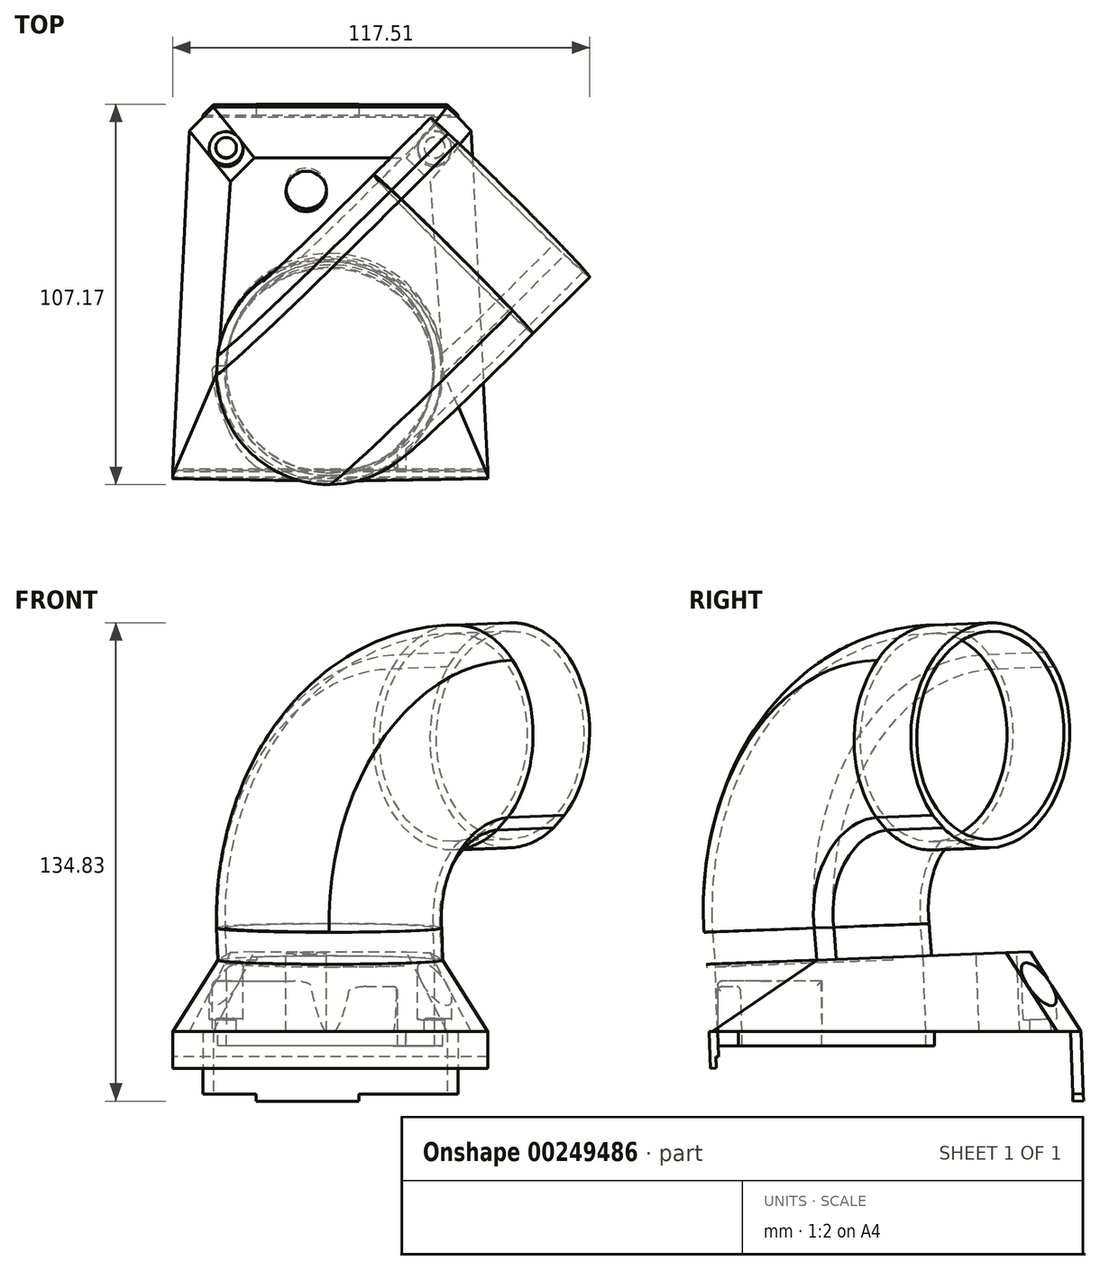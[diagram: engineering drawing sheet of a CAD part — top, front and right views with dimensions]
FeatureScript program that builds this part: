
annotation { "Feature Type Name" : "Feature", "Feature Type Description" : "" }
export const myFeature = defineFeature(function(context is Context, id is Id, definition is map)
    precondition{}
    {
        {
            var Q0;
            Q0=qCreatedBy(makeId("Top.planeOp"),FACE);
            var sketch = newSketch(context, id + "F0", { "sketchPlane" : qUnion([Q0])});
            skLineSegment(sketch, "E0", {"start": v(-32.94, 52.39) * mm, "end": v(32.94, 52.39) * mm});
            skLineSegment(sketch, "E1", {"start": v(32.94, 52.39) * mm, "end": v(39.68, 45.65) * mm});
            skLineSegment(sketch, "E2", {"start": v(39.68, 45.65) * mm, "end": v(44.4, -51.56) * mm});
            skLineSegment(sketch, "E3", {"start": v(43.62, -52.39) * mm, "end": v(-43.62, -52.39) * mm});
            skLineSegment(sketch, "E4", {"start": v(-44.4, -51.56) * mm, "end": v(-39.68, 45.65) * mm});
            skLineSegment(sketch, "E5", {"start": v(-39.68, 45.65) * mm, "end": v(-32.94, 52.39) * mm});
            skLineSegment(sketch, "E6", {"start": v(0, 0) * mm, "end": v(-41.9, 0) * mm, "construction": true});
            skLineSegment(sketch, "E7", {"start": v(0, 0) * mm, "end": v(41.9, 0) * mm, "construction": true});
            skLineSegment(sketch, "E8", {"start": v(0, 0) * mm, "end": v(0, -52.39) * mm, "construction": true});
            skLineSegment(sketch, "E9", {"start": v(0, 0) * mm, "end": v(0, 52.39) * mm, "construction": true});
            skPoint(sketch, "E10", {"position": v(0, -20.66) * mm});
            skPoint(sketch, "E11.visualSharp", {"position": v(-44.45, -52.39) * mm});
            skArc(sketch, "E11.filletArc", {"start": v(-44.4, -51.56) * mm, "mid": v(-44.2, -52.14) * mm, "end": v(-43.62, -52.39) * mm});
            skPoint(sketch, "E12.visualSharp", {"position": v(44.45, -52.39) * mm});
            skArc(sketch, "E12.filletArc", {"start": v(43.62, -52.39) * mm, "mid": v(44.2, -52.14) * mm, "end": v(44.4, -51.56) * mm});
            skSolve(sketch);
        }
        {
            var Q0;
            Q0=qCreatedBy(makeId("Right.planeOp"),FACE);
            var sketch = newSketch(context, id + "F1", { "sketchPlane" : qUnion([Q0])});
            skPoint(sketch, "E13.0", {"position": v(52.39, 0) * mm});
            skPoint(sketch, "E14.0", {"position": v(-51.56, 0) * mm});
            skLineSegment(sketch, "E15", {"start": v(52.39, 0) * mm, "end": v(52.39, 23.02) * mm, "construction": true});
            skLineSegment(sketch, "E16", {"start": v(-51.56, 0) * mm, "end": v(-51.56, 19.05) * mm, "construction": true});
            skSolve(sketch);
        }
        {
            var Q0;
            Q0=qCreatedBy(makeId("Top.planeOp"),FACE);
            cPlane(context, id + "F2", {"entities" : qUnion([Q0]), "cplaneType" : CPlaneType.OFFSET, "offset" : 23.02 * mm, "width" : 152.4 * mm, "height" : 152.4 * mm});
        }
        {
            var Q0;
            Q0=qCreatedBy(id+"F2.planeOp",FACE);
            var sketch = newSketch(context, id + "F3", { "sketchPlane" : qUnion([Q0])});
            skPoint(sketch, "E17.0", {"position": v(0, 52.39) * mm});
            skLineSegment(sketch, "E18", {"start": v(0, 52.39) * mm, "end": v(20.13, 52.39) * mm, "construction": true});
            skSolve(sketch);
        }
        {
            var Q0;
            Q0=sQuery(id+"F3.wireOp",EDGE,"E18");
            var Q1;
            Q1=sQuery(id+"F1.wireOp",VERTEX,"E16.end");
            cPlane(context, id + "F4", {"entities" : qUnion([Q0, Q1]), "cplaneType" : CPlaneType.LINE_ANGLE, "offset" : 25.4 * mm, "angle" : 0 * degree, "width" : 152.4 * mm, "height" : 152.4 * mm});
        }
        {
            var Q0;
            Q0=qCreatedBy(id+"F4.planeOp",FACE);
            var sketch = newSketch(context, id + "F5", { "sketchPlane" : qUnion([Q0])});
            skCircle(sketch, "E19", {"center": v(0, 20.65) * mm, "radius": 29.34 * mm, "construction": true});
            skArc(sketch, "E20", {"start": v(-31.72, 21.31) * mm, "mid": v(0, -11.08) * mm, "end": v(31.72, 21.32) * mm, "construction": true});
            skArc(sketch, "E21", {"start": v(31.72, 21.32) * mm, "mid": v(22.21, 43.3) * mm, "end": v(0.05, 52.37) * mm});
            skLineSegment(sketch, "E22", {"start": v(0, -11.08) * mm, "end": v(0, 49.98) * mm, "construction": true});
            skLineSegment(sketch, "E23", {"start": v(-21.43, -38.9) * mm, "end": v(21.43, -38.9) * mm});
            skLineSegment(sketch, "E24", {"start": v(21.43, -38.9) * mm, "end": v(28.17, -32.17) * mm});
            skLineSegment(sketch, "E25", {"start": v(28.17, -32.17) * mm, "end": v(31.72, 21.32) * mm});
            skLineSegment(sketch, "E26", {"start": v(-21.43, -38.9) * mm, "end": v(-28.16, -32.17) * mm});
            skLineSegment(sketch, "E27", {"start": v(-28.16, -32.17) * mm, "end": v(-31.72, 21.31) * mm});
            skArc(sketch, "E28", {"start": v(-0.04, 52.37) * mm, "mid": v(-22.2, 43.3) * mm, "end": v(-31.72, 21.31) * mm});
            skArc(sketch, "E29", {"start": v(0.05, 52.37) * mm, "mid": v(0, 52.37) * mm, "end": v(-0.04, 52.37) * mm});
            skSolve(sketch);
        }
        {
            var Q0;
            Q0=makeQuery(id+"F0.imprint","IMPRINT",FACE,{"disambiguationData":[TD([[makeQuery(id+"F0.imprint","IMPRINT",EDGE,{"derivedFrom":sQuery(id+"F0.wireOp",EDGE,"E0")}),-1.0]])]});
            var Q1;
            Q1=makeQuery(id+"F5.imprint","IMPRINT",FACE,{"disambiguationData":[TD([[makeQuery(id+"F5.imprint","IMPRINT",EDGE,{"derivedFrom":sQuery(id+"F5.wireOp",EDGE,"E21")}),1.0]])]});
            loft(context, id + "F6", {"sheetProfilesArray" : [{ "sheetProfileEntities" : qUnion([Q0]) }, { "sheetProfileEntities" : qUnion([Q1]) }]});
        }
        {
            var Q0;
            Q0=makeQuery(id+"F6.opLoft","CAP_FACE",FACE,{"disambiguationData":[OSD([makeQuery(id+"F5.imprint","IMPRINT",FACE,{"disambiguationData":[TD([[makeQuery(id+"F5.imprint","IMPRINT",EDGE,{"derivedFrom":sQuery(id+"F5.wireOp",EDGE,"E21")}),1.0]])]})])],"isStart":true});
            var sketch = newSketch(context, id + "F7", { "sketchPlane" : qUnion([Q0])});
            skCircle(sketch, "E30", {"center": v(0, -20.65) * mm, "radius": 29.34 * mm});
            skSolve(sketch);
        }
        {
            var Q0;
            Q0 = qSketchRegion(id + "F7", true);
            extrude(context, id + "F8", {"entities" : qUnion([Q0]), "operationType" : NewBodyOperationType.REMOVE, "endBound" : BoundingType.UP_TO_NEXT, "oppositeDirection" : true, "depth" : 25.4 * mm});
        }
        {
            var Q0;
            Q0=sQuery(id+"F0.wireOp",EDGE,"E3");
            var Q1;
            Q1=makeQuery(id+"F6.opLoft","CAP_FACE",FACE,{"disambiguationData":[OSD([makeQuery(id+"F5.imprint","IMPRINT",FACE,{"disambiguationData":[TD([[makeQuery(id+"F5.imprint","IMPRINT",EDGE,{"derivedFrom":sQuery(id+"F5.wireOp",EDGE,"E21")}),1.0]])]})])],"isStart":true});
            cPlane(context, id + "F9", {"entities" : qUnion([Q0, Q1]), "cplaneType" : CPlaneType.LINE_ANGLE, "offset" : 25.4 * mm, "angle" : 90 * degree, "width" : 152.4 * mm, "height" : 152.4 * mm});
        }
        {
            var Q0;
            Q0=qCreatedBy(id+"F9.planeOp",FACE);
            var sketch = newSketch(context, id + "F10", { "sketchPlane" : qUnion([Q0])});
            skLineSegment(sketch, "E31.0", {"start": v(43.62, 2) * mm, "end": v(-43.62, 2) * mm});
            skEllipticalArc(sketch, "E32.0", {});
            skEllipticalArc(sketch, "E33.0", {});
            skLineSegment(sketch, "E34.bottom", {"start": v(44.4, 1.97) * mm, "end": v(-44.4, 1.97) * mm});
            skLineSegment(sketch, "E34.top", {"start": v(44.4, -8.35) * mm, "end": v(-44.4, -8.35) * mm});
            skLineSegment(sketch, "E34.left", {"start": v(44.4, 1.97) * mm, "end": v(44.4, -8.35) * mm});
            skLineSegment(sketch, "E34.right", {"start": v(-44.4, 1.97) * mm, "end": v(-44.4, -8.35) * mm});
            const initialGuessF10  = {"E32.0": [-0.04361665668816759, 0.001968524113919549, 1, 0, 0.0007937500000000046, 3.0284986367993234e-05, 1.5707963267948966, 3.1902505879491185], "E33.0": [0.04361665668816731, 0.0019685241139195475, 1, 0, 0.0007937500000000028, 3.0284986367993163e-05, 6.234527372820301, 1.5707963267948966]};
            skSetInitialGuess(sketch, initialGuessF10);
            skSolve(sketch);
        }
        {
            var Q0;
            Q0 = qSketchRegion(id + "F10", true);
            extrude(context, id + "F11", {"entities" : qUnion([Q0]), "operationType" : NewBodyOperationType.ADD, "oppositeDirection" : true, "depth" : 2.4 * mm});
        }
        {
            var Q0;
            Q0=makeQuery(id+"F11.opExtrude","CAP_FACE",FACE,{"disambiguationData":[OSD([sQuery(id+"F10.wireOp",EDGE,"E31.0"),sQuery(id+"F10.wireOp",EDGE,"E32.0"),sQuery(id+"F10.wireOp",EDGE,"E33.0"),sQuery(id+"F10.wireOp",EDGE,"E34.top"),sQuery(id+"F10.wireOp",EDGE,"E34.left"),sQuery(id+"F10.wireOp",EDGE,"E34.right")])],"isStart":false});
            cPlane(context, id + "F12", {"entities" : qUnion([Q0]), "cplaneType" : CPlaneType.OFFSET, "offset" : 99.31 * mm, "width" : 152.4 * mm, "height" : 152.4 * mm});
        }
        {
            var Q0;
            Q0=qCreatedBy(id+"F12.planeOp",FACE);
            var sketch = newSketch(context, id + "F13", { "sketchPlane" : qUnion([Q0])});
            skLineSegment(sketch, "E35.0.6", {"start": v(-32.94, -2) * mm, "end": v(32.94, -2) * mm});
            skLineSegment(sketch, "E36.bottom", {"start": v(36.9, -2) * mm, "end": v(-36.9, -2) * mm});
            skLineSegment(sketch, "E36.top", {"start": v(36.9, -19.46) * mm, "end": v(-36.9, -19.46) * mm});
            skLineSegment(sketch, "E36.left", {"start": v(36.9, -2) * mm, "end": v(36.9, -19.46) * mm});
            skLineSegment(sketch, "E36.right", {"start": v(-36.9, -2) * mm, "end": v(-36.9, -19.46) * mm});
            skLineSegment(sketch, "E37", {"start": v(0, -19.46) * mm, "end": v(0, -2) * mm, "construction": true});
            skSolve(sketch);
        }
        {
            var Q0;
            Q0 = qSketchRegion(id + "F13", true);
            var Q1;
            Q1=sQuery(id+"F0.wireOp",VERTEX,"E0.start");
            extrude(context, id + "F14", {"entities" : qUnion([Q0]), "operationType" : NewBodyOperationType.ADD, "endBound" : BoundingType.UP_TO_VERTEX, "endBoundEntityVertex" : qUnion([Q1]), "depth" : 25.4 * mm});
        }
        {
            var Q0;
            Q0=makeQuery(id+"F14.opExtrude","SWEPT_FACE",FACE,{"disambiguationData":[OSD([sQuery(id+"F13.wireOp",EDGE,"E36.left")])]});
            var sketch = newSketch(context, id + "F15", { "sketchPlane" : qUnion([Q0])});
            skLineSegment(sketch, "E38.0", {"start": v(-45.65, 0) * mm, "end": v(-52.39, 0) * mm});
            skLineSegment(sketch, "E39.0.0", {"start": v(-49.4, -0.11) * mm, "end": v(-52.39, 0) * mm});
            skLineSegment(sketch, "E40", {"start": v(-49.4, -0.11) * mm, "end": v(-49.39, 0) * mm});
            skSolve(sketch);
        }
        {
            var Q0;
            Q0 = qSketchRegion(id + "F15", true);
            extrude(context, id + "F16", {"entities" : qUnion([Q0]), "operationType" : NewBodyOperationType.ADD, "oppositeDirection" : true, "depth" : 73.63 * mm});
        }
        {
            var Q0;
            Q0=makeQuery(id+"F14.opExtrude","SWEPT_FACE",FACE,{"disambiguationData":[OSD([sQuery(id+"F13.wireOp",EDGE,"E36.top")])]});
            var sketch = newSketch(context, id + "F17", { "sketchPlane" : qUnion([Q0])});
            skLineSegment(sketch, "E41.0", {"start": v(-35.94, -49.35) * mm, "end": v(-32.94, -52.35) * mm});
            skLineSegment(sketch, "E42", {"start": v(-32.94, -52.35) * mm, "end": v(-36.9, -52.35) * mm});
            skLineSegment(sketch, "E43", {"start": v(-36.9, -52.35) * mm, "end": v(-36.9, -49.35) * mm});
            skLineSegment(sketch, "E44", {"start": v(-36.9, -49.35) * mm, "end": v(-35.94, -49.35) * mm});
            skLineSegment(sketch, "E45.0", {"start": v(32.94, -52.35) * mm, "end": v(35.94, -49.35) * mm});
            skLineSegment(sketch, "E46", {"start": v(32.94, -52.35) * mm, "end": v(36.9, -52.35) * mm});
            skLineSegment(sketch, "E47", {"start": v(36.9, -52.35) * mm, "end": v(36.9, -49.35) * mm});
            skLineSegment(sketch, "E48", {"start": v(36.9, -49.35) * mm, "end": v(35.94, -49.35) * mm});
            skSolve(sketch);
        }
        {
            var Q0;
            Q0 = qSketchRegion(id + "F17", true);
            extrude(context, id + "F18", {"entities" : qUnion([Q0]), "operationType" : NewBodyOperationType.REMOVE, "endBound" : BoundingType.UP_TO_NEXT, "oppositeDirection" : true, "depth" : 25.4 * mm});
        }
        {
            var Q0;
            Q0=makeQuery(id+"F11.opExtrude","SWEPT_FACE",FACE,{"disambiguationData":[OSD([sQuery(id+"F10.wireOp",EDGE,"E34.top")])]});
            var sketch = newSketch(context, id + "F19", { "sketchPlane" : qUnion([Q0])});
            skEllipticalArc(sketch, "E49.0", {});
            skLineSegment(sketch, "E50.0", {"start": v(-44.4, 51.52) * mm, "end": v(-39.68, -45.62) * mm});
            skLineSegment(sketch, "E51", {"start": v(-44.4, 49.96) * mm, "end": v(-44.33, 49.96) * mm});
            skLineSegment(sketch, "E52", {"start": v(-44.4, 49.96) * mm, "end": v(-44.4, 51.52) * mm});
            skLineSegment(sketch, "E53", {"start": v(-44.4, 51.52) * mm, "end": v(-44.4, 52.35) * mm});
            skLineSegment(sketch, "E54", {"start": v(-44.4, 52.35) * mm, "end": v(-43.62, 52.35) * mm});
            const initialGuessF19  = {"E49.0": [-0.04361665668816758, 0.051556182479654336, -1, 0, 0.0007937500000000046, 0.000793172038148533, 4.712388980384686, 0.04865793435924814]};
            skSetInitialGuess(sketch, initialGuessF19);
            skSolve(sketch);
        }
        {
            var Q0;
            Q0=sQuery(id+"F0.wireOp",VERTEX,"E10");
            var Q1;
            Q1=qCreatedBy(id+"F9.planeOp",FACE);
            cPlane(context, id + "F20", {"entities" : qUnion([Q0, Q1]), "cplaneType" : CPlaneType.PLANE_POINT, "offset" : 25.4 * mm, "width" : 152.4 * mm, "height" : 152.4 * mm});
        }
        {
            var Q0;
            Q0=qCreatedBy(id+"F20.planeOp",FACE);
            var Q1;
            Q1=qCreatedBy(makeId("Right.planeOp"),FACE);
            cPlane(context, id + "F21", {"entities" : qUnion([Q0, Q1]), "cplaneType" : CPlaneType.MID_PLANE, "offset" : 25.4 * mm, "flipAlignment" : true, "width" : 152.4 * mm, "height" : 152.4 * mm});
        }
        {
            var Q0;
            Q0=qCreatedBy(id+"F21.planeOp",FACE);
            var sketch = newSketch(context, id + "F22", { "sketchPlane" : qUnion([Q0])});
            skLineSegment(sketch, "E55.0", {"start": v(-45, 18.6) * mm, "end": v(13.58, 21.77) * mm, "construction": true});
            skLineSegment(sketch, "E56", {"start": v(-15.71, 20.19) * mm, "end": v(-16.24, 30.05) * mm});
            skLineSegment(sketch, "E57", {"start": v(34.48, 83.6) * mm, "end": v(57.06, 83.6) * mm});
            skPoint(sketch, "E58.visualSharp", {"position": v(-19.14, 83.6) * mm});
            skArc(sketch, "E58.filletArc", {"start": v(34.48, 83.6) * mm, "mid": v(-2.4, 67.73) * mm, "end": v(-16.24, 30.05) * mm});
            skSolve(sketch);
        }
        {
            var Q0;
            Q0=makeQuery(id+"F6.opLoft","CAP_FACE",FACE,{"disambiguationData":[OSD([makeQuery(id+"F5.imprint","IMPRINT",FACE,{"disambiguationData":[TD([[makeQuery(id+"F5.imprint","IMPRINT",EDGE,{"derivedFrom":sQuery(id+"F5.wireOp",EDGE,"E21")}),1.0]])]})])],"isStart":true});
            var sketch = newSketch(context, id + "F23", { "sketchPlane" : qUnion([Q0])});
            skCircle(sketch, "E59.0", {"center": v(0, -20.65) * mm, "radius": 29.34 * mm});
            skFitSpline(sketch, "E60.0", {"points": [v(-31.72, -21.31) * mm, v(-31.67, -23.37) * mm, v(-31.43, -25.4) * mm, v(-31, -27.4) * mm, v(-30.56, -29.4) * mm, v(-29.93, -31.36) * mm, v(-29.12, -33.24) * mm, v(-28.3, -35.12) * mm, v(-27.31, -36.91) * mm, v(-26.15, -38.6) * mm, v(-25, -40.3) * mm, v(-23.68, -41.86) * mm, v(-22.2, -43.3) * mm, v(-20.74, -44.74) * mm, v(-19.15, -46.02) * mm, v(-17.44, -47.15) * mm, v(-15.72, -48.28) * mm, v(-13.91, -49.23) * mm, v(-12.01, -50.01) * mm, v(-10.11, -50.79) * mm, v(-8.16, -51.38) * mm, v(-6.14, -51.77) * mm, v(-4.13, -52.17) * mm, v(-2.1, -52.37) * mm, v(-0.04, -52.37) * mm]});
            skCircle(sketch, "E61", {"center": v(0, -20.65) * mm, "radius": 31.72 * mm});
            skSolve(sketch);
        }
        {
            var Q0;
            Q0=makeQuery(id+"F23.imprint","IMPRINT",FACE,{"disambiguationData":[TD([[makeQuery(id+"F23.imprint","IMPRINT",EDGE,{"derivedFrom":sQuery(id+"F23.wireOp",EDGE,"E59.0")}),-1.0]])]});
            var Q1;
            Q1=sQuery(id+"F22.wireOp",EDGE,"E56");
            var Q2;
            Q2=sQuery(id+"F22.wireOp",EDGE,"E58.filletArc");
            var Q3;
            Q3=sQuery(id+"F22.wireOp",EDGE,"E57");
            sweep(context, id + "F24", {"operationType" : NewBodyOperationType.ADD, "profiles" : qUnion([Q0]), "path" : qUnion([Q1, Q2, Q3])});
        }
        {
            var Q0;
            {var subQ1=sQuery(id+"F5.wireOp",EDGE,"E24");var subQ2=sQuery(id+"F5.wireOp",EDGE,"E23");var subQ5=sQuery(id+"F5.wireOp",EDGE,"E26");Q0=makeQuery(id+"F23.imprint","IMPRINT",FACE,{"disambiguationData":[TD([[makeQuery(id+"F23.imprint","IMPRINT",EDGE,{"derivedFrom":makeQuery(id+"F6.opLoft","MID_CAP_EDGE",EDGE,{"disambiguationData":[OSD([subQ2,subQ1,subQ5])],"capPos":1.0})}),1.0]])]});}
            var sketch = newSketch(context, id + "F25", { "sketchPlane" : qUnion([Q0])});
            skLineSegment(sketch, "E62.0", {"start": v(-44.4, -51.52) * mm, "end": v(-39.68, 45.62) * mm, "construction": true});
            skLineSegment(sketch, "E63.0", {"start": v(39.68, 45.62) * mm, "end": v(44.4, -51.52) * mm, "construction": true});
            skLineSegment(sketch, "E64.0", {"start": v(35.94, 49.35) * mm, "end": v(-35.94, 49.35) * mm, "construction": true});
            skLineSegment(sketch, "E65", {"start": v(-39.9, 40.97) * mm, "end": v(39.9, 40.97) * mm, "construction": true});
            skCircle(sketch, "E66", {"center": v(-29.36, 40.97) * mm, "radius": 2.92 * mm});
            skCircle(sketch, "E67", {"center": v(29.39, 40.97) * mm, "radius": 2.92 * mm});
            skSolve(sketch);
        }
        {
            var Q0;
            Q0 = qSketchRegion(id + "F25", true);
            var Q1;
            Q1=makeQuery(id+"F6.opLoft","CAP_FACE",FACE,{"disambiguationData":[OSD([makeQuery(id+"F0.imprint","IMPRINT",FACE,{"disambiguationData":[TD([[makeQuery(id+"F0.imprint","IMPRINT",EDGE,{"derivedFrom":sQuery(id+"F0.wireOp",EDGE,"E0")}),-1.0]])]})])],"isStart":true});
            extrude(context, id + "F26", {"entities" : qUnion([Q0]), "operationType" : NewBodyOperationType.REMOVE, "endBound" : BoundingType.UP_TO_SURFACE, "oppositeDirection" : true, "endBoundEntityFace" : qUnion([Q1]), "depth" : 25.4 * mm});
        }
        {
            var Q0;
            {var subQ1=sQuery(id+"F5.wireOp",EDGE,"E24");var subQ2=sQuery(id+"F5.wireOp",EDGE,"E23");var subQ5=sQuery(id+"F5.wireOp",EDGE,"E26");Q0=makeQuery(id+"F23.imprint","IMPRINT",FACE,{"disambiguationData":[TD([[makeQuery(id+"F23.imprint","IMPRINT",EDGE,{"derivedFrom":makeQuery(id+"F6.opLoft","MID_CAP_EDGE",EDGE,{"disambiguationData":[OSD([subQ2,subQ1,subQ5])],"capPos":1.0})}),1.0]])]});}
            var sketch = newSketch(context, id + "F27", { "sketchPlane" : qUnion([Q0])});
            skCircle(sketch, "E68.0", {"center": v(-29.36, 40.97) * mm, "radius": 2.92 * mm});
            skCircle(sketch, "E69.0", {"center": v(29.39, 40.97) * mm, "radius": 2.92 * mm});
            skCircle(sketch, "E70", {"center": v(-29.36, 40.97) * mm, "radius": 4.76 * mm});
            skCircle(sketch, "E71", {"center": v(29.39, 40.97) * mm, "radius": 4.76 * mm});
            skSolve(sketch);
        }
        {
            var Q0;
            Q0 = qSketchRegion(id + "F27", true);
            extrude(context, id + "F28", {"entities" : qUnion([Q0]), "operationType" : NewBodyOperationType.REMOVE, "oppositeDirection" : true, "depth" : 19.05 * mm});
        }
        {
            var Q0;
            Q0=makeQuery(id+"F6.opLoft","CAP_FACE",FACE,{"disambiguationData":[OSD([makeQuery(id+"F5.imprint","IMPRINT",FACE,{"disambiguationData":[TD([[makeQuery(id+"F5.imprint","IMPRINT",EDGE,{"derivedFrom":sQuery(id+"F5.wireOp",EDGE,"E21")}),1.0]])]})])],"isStart":true});
            var sketch = newSketch(context, id + "F29", { "sketchPlane" : qUnion([Q0])});
            skLineSegment(sketch, "E72.0", {"start": v(-28.16, 32.17) * mm, "end": v(-31.35, -15.8) * mm});
            skLineSegment(sketch, "E73.0", {"start": v(31.35, -15.8) * mm, "end": v(28.17, 32.17) * mm});
            skLineSegment(sketch, "E74.0", {"start": v(21.43, 38.9) * mm, "end": v(-21.43, 38.9) * mm});
            skLineSegment(sketch, "E75", {"start": v(-28.35, 29.38) * mm, "end": v(28.35, 29.38) * mm, "construction": true});
            skCircle(sketch, "E76", {"center": v(-6.76, 29.38) * mm, "radius": 5.72 * mm});
            skSolve(sketch);
        }
        {
            var Q0;
            Q0=makeQuery(id+"F29.imprint","IMPRINT",FACE,{"disambiguationData":[TD([[makeQuery(id+"F29.imprint","IMPRINT",EDGE,{"derivedFrom":sQuery(id+"F29.wireOp",EDGE,"E76")}),1.0]])]});
            var Q1;
            Q1 = qConstructionFilter(qBodyType(qCreatedBy(id + "F29" ,EDGE), BodyType.WIRE), ConstructionObject.NO);
            var Q2;
            Q2=makeQuery(id+"F6.opLoft","CAP_FACE",FACE,{"disambiguationData":[OSD([makeQuery(id+"F0.imprint","IMPRINT",FACE,{"disambiguationData":[TD([[makeQuery(id+"F0.imprint","IMPRINT",EDGE,{"derivedFrom":sQuery(id+"F0.wireOp",EDGE,"E0")}),-1.0]])]})])],"isStart":true});
            extrude(context, id + "F30", {"entities" : qUnion([Q0]), "operationType" : NewBodyOperationType.REMOVE, "surfaceEntities" : qUnion([Q1]), "endBound" : BoundingType.UP_TO_SURFACE, "oppositeDirection" : true, "endBoundEntityFace" : qUnion([Q2]), "depth" : 25.4 * mm});
        }
        {
            var Q0;
            Q0=makeQuery(id+"F0.imprint","IMPRINT",FACE,{"disambiguationData":[TD([[makeQuery(id+"F0.imprint","IMPRINT",EDGE,{"derivedFrom":sQuery(id+"F0.wireOp",EDGE,"E0")}),-1.0]])]});
            var sketch = newSketch(context, id + "F31", { "sketchPlane" : qUnion([Q0])});
            skEllipticalArc(sketch, "E77.0", {});
            skArc(sketch, "E78", {"start": v(21.32, -44.15) * mm, "mid": v(12.85, 8.34) * mm, "end": v(-31.72, -20.66) * mm});
            skLineSegment(sketch, "E79", {"start": v(-29.34, -20.66) * mm, "end": v(-31.72, -20.66) * mm});
            skLineSegment(sketch, "E80.0", {"start": v(1.16, -50) * mm, "end": v(44.33, -50) * mm, "construction": true});
            skLineSegment(sketch, "E81", {"start": v(44.33, -50) * mm, "end": v(18.93, -50) * mm});
            skLineSegment(sketch, "E82", {"start": v(18.93, -50) * mm, "end": v(18.93, -43.09) * mm});
            skPoint(sketch, "E83.orphan", {"position": v(-1.16, -50) * mm});
            skLineSegment(sketch, "E84", {"start": v(21.32, -44.15) * mm, "end": v(21.32, -50) * mm});
            skLineSegment(sketch, "E85", {"start": v(21.32, -50) * mm, "end": v(18.93, -50) * mm});
            const initialGuessF31  = {"E77.0": [0, -0.02066289999999782, 0, -1, 0.02935837703552461, 0.029337, 0.7015266646909257, 4.71238898038469]};
            skSetInitialGuess(sketch, initialGuessF31);
            skSolve(sketch);
        }
        {
            var Q0;
            Q0 = qSketchRegion(id + "F31", true);
            extrude(context, id + "F32", {"entities" : qUnion([Q0]), "operationType" : NewBodyOperationType.ADD, "oppositeDirection" : true, "depth" : 3.97 * mm});
        }
        {
            var Q0;
            Q0=makeQuery(id+"F11.opExtrude","SWEPT_FACE",FACE,{"disambiguationData":[OSD([sQuery(id+"F10.wireOp",EDGE,"E34.top")])]});
            var sketch = newSketch(context, id + "F33", { "sketchPlane" : qUnion([Q0])});
            skLineSegment(sketch, "E86.bottom", {"start": v(44.4, 49.96) * mm, "end": v(-44.4, 49.96) * mm});
            skLineSegment(sketch, "E86.top", {"start": v(44.4, 50.76) * mm, "end": v(-44.4, 50.76) * mm});
            skLineSegment(sketch, "E86.left", {"start": v(44.4, 49.96) * mm, "end": v(44.4, 50.76) * mm});
            skLineSegment(sketch, "E86.right", {"start": v(-44.4, 49.96) * mm, "end": v(-44.4, 50.76) * mm});
            skSolve(sketch);
        }
        {
            var Q0;
            Q0 = qSketchRegion(id + "F33", true);
            extrude(context, id + "F34", {"entities" : qUnion([Q0]), "operationType" : NewBodyOperationType.REMOVE, "oppositeDirection" : true, "depth" : 3.17 * mm});
        }
        {
            var Q0;
            Q0=makeQuery(id+"F14.opExtrude","SWEPT_FACE",FACE,{"disambiguationData":[OSD([sQuery(id+"F13.wireOp",EDGE,"E36.top")])]});
            var sketch = newSketch(context, id + "F35", { "sketchPlane" : qUnion([Q0])});
            skLineSegment(sketch, "E87.bottom", {"start": v(8, -52.35) * mm, "end": v(-20.96, -52.35) * mm});
            skLineSegment(sketch, "E87.top", {"start": v(8, -49.35) * mm, "end": v(-20.96, -49.35) * mm});
            skLineSegment(sketch, "E87.left", {"start": v(8, -52.35) * mm, "end": v(8, -49.35) * mm});
            skLineSegment(sketch, "E87.right", {"start": v(-20.96, -52.35) * mm, "end": v(-20.96, -49.35) * mm});
            skSolve(sketch);
        }
        {
            var Q0;
            Q0 = qSketchRegion(id + "F35", true);
            extrude(context, id + "F36", {"entities" : qUnion([Q0]), "operationType" : NewBodyOperationType.ADD, "depth" : 2.03 * mm});
        }
        {
            var Q0;
            Q0=makeQuery(id+"F0.imprint","IMPRINT",FACE,{"disambiguationData":[TD([[makeQuery(id+"F0.imprint","IMPRINT",EDGE,{"derivedFrom":sQuery(id+"F0.wireOp",EDGE,"E0")}),-1.0]])]});
            var sketch = newSketch(context, id + "F37", { "sketchPlane" : qUnion([Q0])});
            skLineSegment(sketch, "E88.0", {"start": v(-17.51, -50) * mm, "end": v(-1.16, -50) * mm});
            skEllipticalArc(sketch, "E89.0", {});
            skArc(sketch, "E90", {"start": v(-33.34, -20.66) * mm, "mid": v(-32.75, -26.9) * mm, "end": v(-31, -32.91) * mm});
            skLineSegment(sketch, "E91", {"start": v(-29.34, -20.66) * mm, "end": v(-33.34, -20.66) * mm});
            skLineSegment(sketch, "E92", {"start": v(-28.82, -38.45) * mm, "end": v(-31, -32.91) * mm});
            skLineSegment(sketch, "E93", {"start": v(-21.88, -48.27) * mm, "end": v(-21.69, -48.44) * mm});
            skArc(sketch, "E94.filletArc", {"start": v(-28.82, -38.45) * mm, "mid": v(-25.94, -43.77) * mm, "end": v(-21.88, -48.27) * mm});
            skPoint(sketch, "E95.newPointB", {"position": v(-44.33, -50) * mm});
            skArc(sketch, "E95.filletArc", {"start": v(-21.69, -48.44) * mm, "mid": v(-19.74, -49.6) * mm, "end": v(-17.51, -50) * mm});
            const initialGuessF37  = {"E89.0": [0, -0.02066289999999782, 0, -1, 0.02935837703552461, 0.029337, 4.71238898038469, 6.243498931064981]};
            skSetInitialGuess(sketch, initialGuessF37);
            skSolve(sketch);
        }
        {
            var Q0;
            Q0 = qSketchRegion(id + "F37", true);
            extrude(context, id + "F38", {"entities" : qUnion([Q0]), "operationType" : NewBodyOperationType.REMOVE, "depth" : 14.29 * mm});
        }
        {
            var Q0;
            Q0=makeQuery(id+"F0.imprint","IMPRINT",FACE,{"disambiguationData":[TD([[makeQuery(id+"F0.imprint","IMPRINT",EDGE,{"derivedFrom":sQuery(id+"F0.wireOp",EDGE,"E0")}),-1.0]])]});
            var sketch = newSketch(context, id + "F39", { "sketchPlane" : qUnion([Q0])});
            skLineSegment(sketch, "E96.0", {"start": v(18.93, -50) * mm, "end": v(18.93, -43.09) * mm});
            skEllipticalArc(sketch, "E97.0", {});
            skLineSegment(sketch, "E98.0", {"start": v(1.16, -50) * mm, "end": v(18.93, -50) * mm});
            const initialGuessF39  = {"E97.0": [0, -0.02066289999999782, 0, -1, 0.02935837703552461, 0.029337, 0.03968637611464158, 0.7015266646909262]};
            skSetInitialGuess(sketch, initialGuessF39);
            skSolve(sketch);
        }
        {
            var Q0;
            Q0 = qSketchRegion(id + "F39", true);
            extrude(context, id + "F40", {"entities" : qUnion([Q0]), "operationType" : NewBodyOperationType.REMOVE, "depth" : 12.7 * mm});
        }
        {
            var Q0;
            Q0=makeQuery(id+"F32.boolean.opBoolean","INTERSECT",EDGE,{"derivedFrom":[makeQuery(id+"F11.opExtrude","CAP_FACE",FACE,{"disambiguationData":[OSD([sQuery(id+"F10.wireOp",EDGE,"E31.0"),sQuery(id+"F10.wireOp",EDGE,"E32.0"),sQuery(id+"F10.wireOp",EDGE,"E33.0"),sQuery(id+"F10.wireOp",EDGE,"E34.top"),sQuery(id+"F10.wireOp",EDGE,"E34.left"),sQuery(id+"F10.wireOp",EDGE,"E34.right")])],"isStart":false}),makeQuery(id+"F32.opExtrude","SWEPT_FACE",FACE,{"disambiguationData":[OSD([sQuery(id+"F31.wireOp",EDGE,"E82")])]})]});
            var Q1;
            Q1=makeQuery(id+"F40.boolean.opBoolean","COPY",EDGE,{"derivedFrom":makeQuery(id+"F40.opExtrude","CAP_EDGE",EDGE,{"disambiguationData":[OSD([sQuery(id+"F39.wireOp",EDGE,"E98.0")])],"isStart":false})});
            var Q2;
            Q2=makeQuery(id+"F40.boolean.opBoolean","COPY",EDGE,{"derivedFrom":makeQuery(id+"F40.opExtrude","CAP_EDGE",EDGE,{"disambiguationData":[OSD([sQuery(id+"F39.wireOp",EDGE,"E96.0")])],"isStart":false})});
            var Q3;
            Q3=makeQuery(id+"F38.boolean.opBoolean","COPY",EDGE,{"derivedFrom":makeQuery(id+"F38.opExtrude","CAP_EDGE",EDGE,{"disambiguationData":[OSD([sQuery(id+"F37.wireOp",EDGE,"E88.0")])],"isStart":false})});
            var Q4;
            Q4=makeQuery(id+"F38.boolean.opBoolean","COPY",EDGE,{"derivedFrom":makeQuery(id+"F38.opExtrude","SWEPT_EDGE",EDGE,{"disambiguationData":[OSD([sQuery(id+"F37.wireOp",EDGE,"E90"),sQuery(id+"F37.wireOp",EDGE,"E91")])]})});
            fillet(context, id + "F41", {"entities" : qUnion([Q0, Q1, Q2, Q3, Q4]), "radius" : 1.27 * mm, "tangentPropagation" : true, "allowEdgeOverflow" : false});
        }
    });
